# Revit family: SideUnit-60cm-WithDrawer-Vitra-OriginSeries-65698+65699+65700
name_source: partatom
category: Furniture Systems
revit_build: Autodesk Revit 2017 (Build: 20160225_1515(x64)
units: mm (PartAtom-declared; Revit-internal decimal feet)

## family parameters
Cut with Voids When Loaded = No
Host = Face
OmniClass Number = 23.40.00.00
OmniClass Title = Equipment and Furnishings
Part Type = Normal
Room Calculation Point = No
Round Connector Dimension = Use Diameter
Shared = Yes

## types (3) — shared parameters
BIMobject category = Bathroom compound units
Brand = VitrA
Default Elevation = 660 mm
Design country = Turkey
IFC Classification = Furniture
Installation instructions = https://www.vitraglobal.com
Main Material = Wood
Manufacturer = Vitra
Manufacturer name = Vitra
Masterformat 2014 Code = 13 42 13
Masterformat 2014 Description = Bathroom Unit Modules
Mounting type = Wall Mounted
NBS Referans Code = 35-75-08
NBS Referans Description = Bathroom Cabinets
Nominal Depth (mm) = 480 mm  [stored 1.5748 ft]
Nominal Height (mm) = 295 mm
Nominal Width (mm) = 600 mm
OmniClass Code = 23-31 25 13
OmniClass Description = Bathroom Cabinets
Product Guid = https://www.vitraglobal.com
Product certification = https://www.vitraglobal.com
Product family = Origin
Product group = Short Side Unit
Product url = https://www.vitraglobal.com
Technical description = https://www.vitraglobal.com
UNSPSC Description = Bathroom Cabinets
URL = https://vitraglobal.com
Uniclass 1.4 Code = L8241
Uniclass 1.4 Description = Bathroom Cabinets
Uniclass 2.0 Code = PR-35-75-08
Uniclass 2.0 Description = Bathroom Cabinets
Uniclass 2015 Code = Pr_40_20_93
Uniclass 2015 Name = Wash basins, sinks and troughs
Uniformat II Code = E20
Uniformat II Description = FURNISHINGS
Warranty Period (Year) = 2
Youtube = https://www.youtube.com

## per-type parameters (varying)
| type | Article No. (default) | Color | Description | Model | Primary Material | Product SKU | Product data url |
| SideUnit-60cm-Vitra-OriginSeries-65698 | 65698 | Patterned black oak | Origin short side unit with drawer - 60cm - patterned black oak | 65698 | Patterned Black Oak | 65698 | https://www.bimobject.com |
| SideUnit-60cm-Vitra-OriginSeries-65699 | 65699 | Elm | Origin short side unit with drawer - 60cm - Elm | 65699 | Elm | 65699 |  |
| SideUnit-60cm-Vitra-OriginSeries-65700 | 65700 | Flat Oak | Origin short side unit with drawer - 60cm - Flat Oak | 65700 | Flat Oak | 65700 |  |

note: [stored X ft] marks values corroborated as IEEE doubles in the binary element streams (Revit-internal decimal feet)

## geometry (parser evidence)
native form markers: Sweep x2
no freeform markers — native parametric forms only
